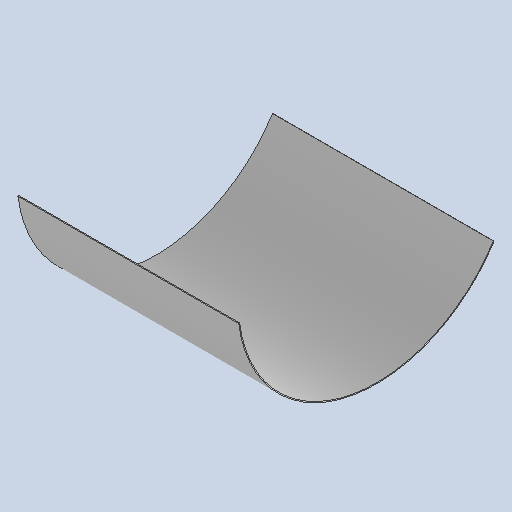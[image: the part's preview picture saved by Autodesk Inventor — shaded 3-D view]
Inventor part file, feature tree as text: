
AUTODESK INVENTOR PART (.ipt)
format: ipt  version: 2025 (Build 290162010, 162A)  size: 195,584 bytes
history: native  units: mm
features: sheet_metal_op x3, other x3, sketch x1
ambient origin geometry x8: Origin, YZ Plane, XZ Plane, XY Plane, X Axis, Y Axis, Z Axis, Center Point
bodies: Body1 (feature_tree)
feature tree (7):
  sheet_metal_op  "Contour Flange1"
  other  "A-Side Definition"
  sketch  "Sketch7"  dims[d54=300.0mm d55=2.0mm d56=2.0mm d57=1.0mm d58=4.0mm d59=2.75mm d60=480.0mm d61=2.75mm d62=2.0mm d63=8.0mm d64=2.0mm d65=2.75mm d66=121.350938mm d68=1.291893mm d69=595.0mm d70=140.0mm d72=100.0mm d74=25.790564mm]
  other  "Plate6"
  sheet_metal_op  "Bend5"
  sheet_metal_op  "Corner5"
  other  "Definition1"
